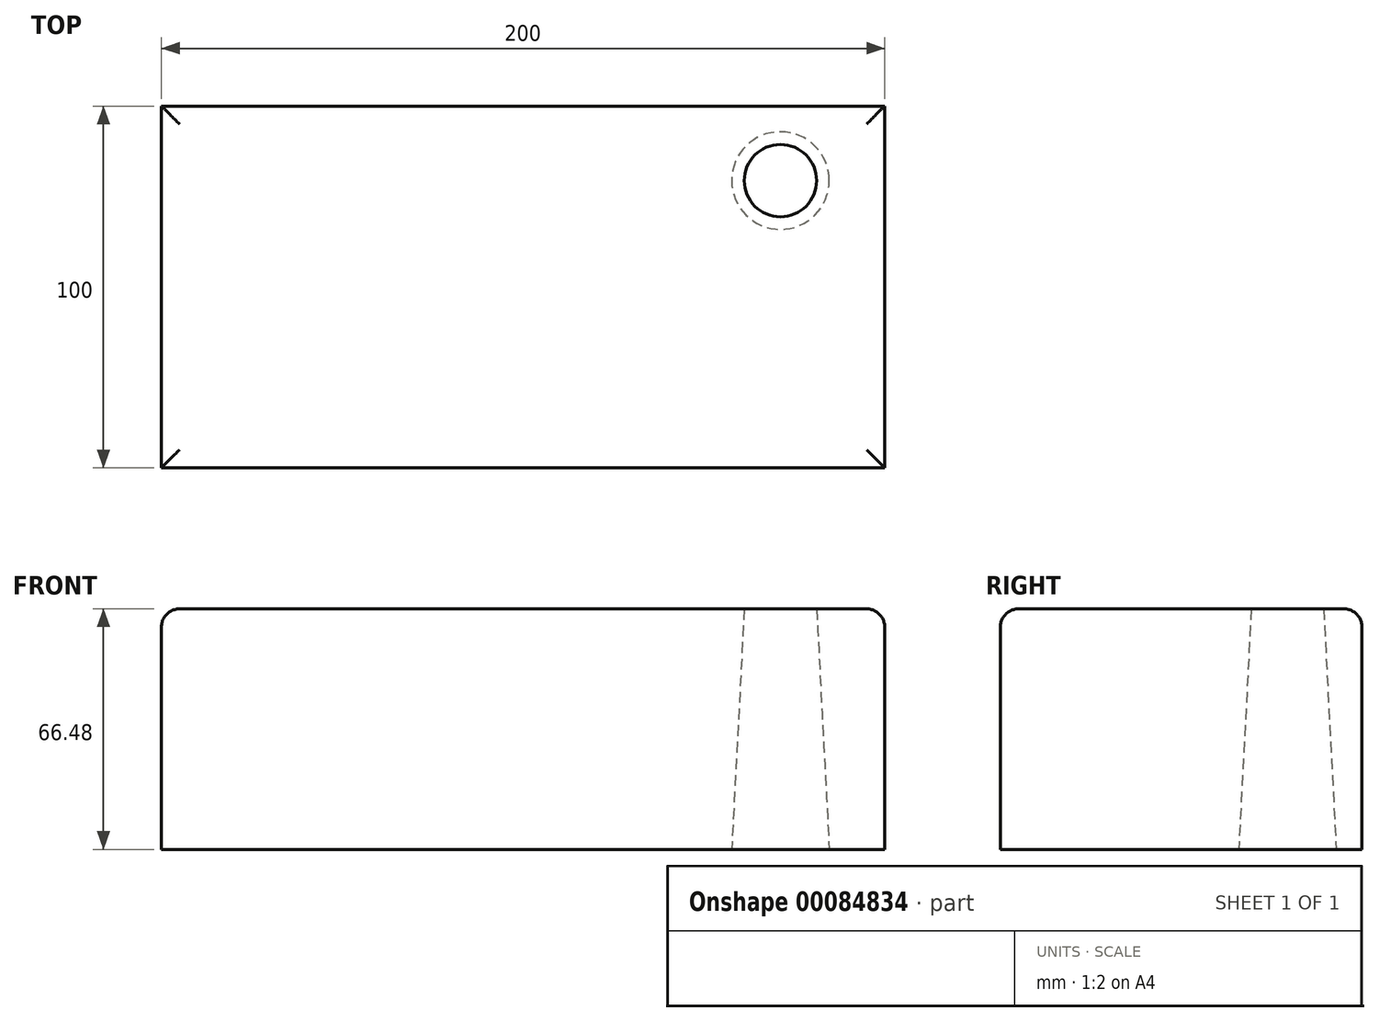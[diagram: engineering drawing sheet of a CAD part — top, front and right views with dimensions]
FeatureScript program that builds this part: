
annotation { "Feature Type Name" : "Feature", "Feature Type Description" : "" }
export const myFeature = defineFeature(function(context is Context, id is Id, definition is map)
    precondition{}
    {
        {
            var Q0;
            Q0=qCreatedBy(makeId("Top.planeOp"),FACE);
            var sketch = newSketch(context, id + "F0", { "sketchPlane" : qUnion([Q0])});
            skLineSegment(sketch, "E0.bottom", {"start": v(0, 0) * mm, "end": v(200, 0) * mm});
            skLineSegment(sketch, "E0.top", {"start": v(0, 100) * mm, "end": v(200, 100) * mm});
            skLineSegment(sketch, "E0.left", {"start": v(0, 0) * mm, "end": v(0, 100) * mm});
            skLineSegment(sketch, "E0.right", {"start": v(200, 0) * mm, "end": v(200, 100) * mm});
            skSolve(sketch);
        }
        {
            var Q0;
            Q0 = qSketchRegion(id + "F0", true);
            extrude(context, id + "F1", {"entities" : qUnion([Q0]), "depth" : 66.48 * mm});
        }
        {
            var Q0;
            Q0=makeQuery(id+"F1.opExtrude","CAP_FACE",FACE,{"disambiguationData":[OSD([sQuery(id+"F0.wireOp",EDGE,"E0.bottom"),sQuery(id+"F0.wireOp",EDGE,"E0.top"),sQuery(id+"F0.wireOp",EDGE,"E0.left"),sQuery(id+"F0.wireOp",EDGE,"E0.right")])],"isStart":false});
            var sketch = newSketch(context, id + "F2", { "sketchPlane" : qUnion([Q0])});
            skCircle(sketch, "E1", {"center": v(171.18, 79.39) * mm, "radius": 10 * mm});
            skSolve(sketch);
        }
        {
            var Q0;
            Q0 = qSketchRegion(id + "F2", true);
            extrude(context, id + "F3", {"entities" : qUnion([Q0]), "operationType" : NewBodyOperationType.REMOVE, "endBound" : BoundingType.THROUGH_ALL, "oppositeDirection" : true, "depth" : 25 * mm, "hasDraft" : true, "draftAngle" : 3 * degree});
        }
        {
            var Q0;
            Q0=makeQuery(id+"F1.opExtrude","CAP_EDGE",EDGE,{"disambiguationData":[OSD([sQuery(id+"F0.wireOp",EDGE,"E0.top")])],"isStart":false});
            var Q1;
            Q1=makeQuery(id+"F1.opExtrude","CAP_EDGE",EDGE,{"disambiguationData":[OSD([sQuery(id+"F0.wireOp",EDGE,"E0.bottom")])],"isStart":false});
            var Q2;
            Q2=makeQuery(id+"F1.opExtrude","CAP_EDGE",EDGE,{"disambiguationData":[OSD([sQuery(id+"F0.wireOp",EDGE,"E0.right")])],"isStart":false});
            var Q3;
            Q3=makeQuery(id+"F1.opExtrude","CAP_EDGE",EDGE,{"disambiguationData":[OSD([sQuery(id+"F0.wireOp",EDGE,"E0.left")])],"isStart":false});
            fillet(context, id + "F4", {"entities" : qUnion([Q0, Q1, Q2, Q3]), "radius" : 5 * mm, "tangentPropagation" : true, "allowEdgeOverflow" : false});
        }
    });
